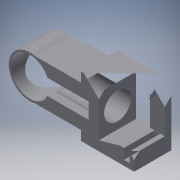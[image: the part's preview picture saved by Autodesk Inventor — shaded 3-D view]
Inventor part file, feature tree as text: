
AUTODESK INVENTOR PART (.ipt)
format: ipt  version: 2016 (Build 200138000, 138)  size: 249,344 bytes
history: native  units: mm
features: extrude x10, sketch x10, projected_geometry x2, reference x2
ambient origin geometry x8: Origin, YZ Plane, XZ Plane, XY Plane, X Axis, Y Axis, Z Axis, Center Point
bodies: Solid1 (feature_tree)
feature tree (24):
  extrude  "Extrusion1"  Depth=7.0mm
  extrude  "Extrusion2"  Depth=14.5mm TaperAngle=0.0deg
  extrude  "Extrusion3"  Depth=3.749999mm
  extrude  "Extrusion4"  Depth=20.0mm
  extrude  "Extrusion5"  Depth=15.0mm
  extrude  "Extrusion6"  Depth=14.0mm
  extrude  "Extrusion7"  Depth=10.5mm
  extrude  "Extrusion9"  Depth=1.0mm TaperAngle=0.0deg
  extrude  "Extrusion10"  Depth=3.0mm
  extrude  "Extrusion12"  Depth=3.0mm
  sketch  "Sketch1"  dims[d0=23.495mm d1=7.0mm]
  sketch  "Sketch2"  dims[d8=6.0mm d10=15.0mm d11=14.999996mm d16=14.5mm d17=0.0mm]
  sketch  "Sketch3"  dims[d18=3.749998mm d19=3.749999mm]
  sketch  "Sketch4"  dims[d20=20.0mm d21=0.0mm d22=16.5mm]
  sketch  "Sketch5"  dims[d23=14.5mm d24=0.0mm d25=15.0mm]
  sketch  "Sketch6"  dims[d26=10.5mm d27=0.0mm d28=14.0mm]
  sketch  "Sketch7"  dims[d29=10.5mm d30=0.0mm d31=10.5mm]
  sketch  "Sketch9"  dims[d32=30.0mm d33=0.0mm d34=1.0mm d35=0.0mm]
  sketch  "Sketch10"  dims[d39=3.0mm d40=3.0mm]
  projected_geometry  "Projected Loop1"
  projected_geometry  "Projected Loop2"
  reference  "Reference2"
  sketch  "Sketch12"  dims[d41=3.0mm d42=3.0mm d43=20.0mm d44=3.0mm d45=0.0mm d46=3.0mm d47=0.0mm d50=16.5mm d51=0.25mm d52=0.25mm d53=0.25mm d54=2.0mm d55=6.99mm d56=0.0mm]
  reference  "Reference3"
